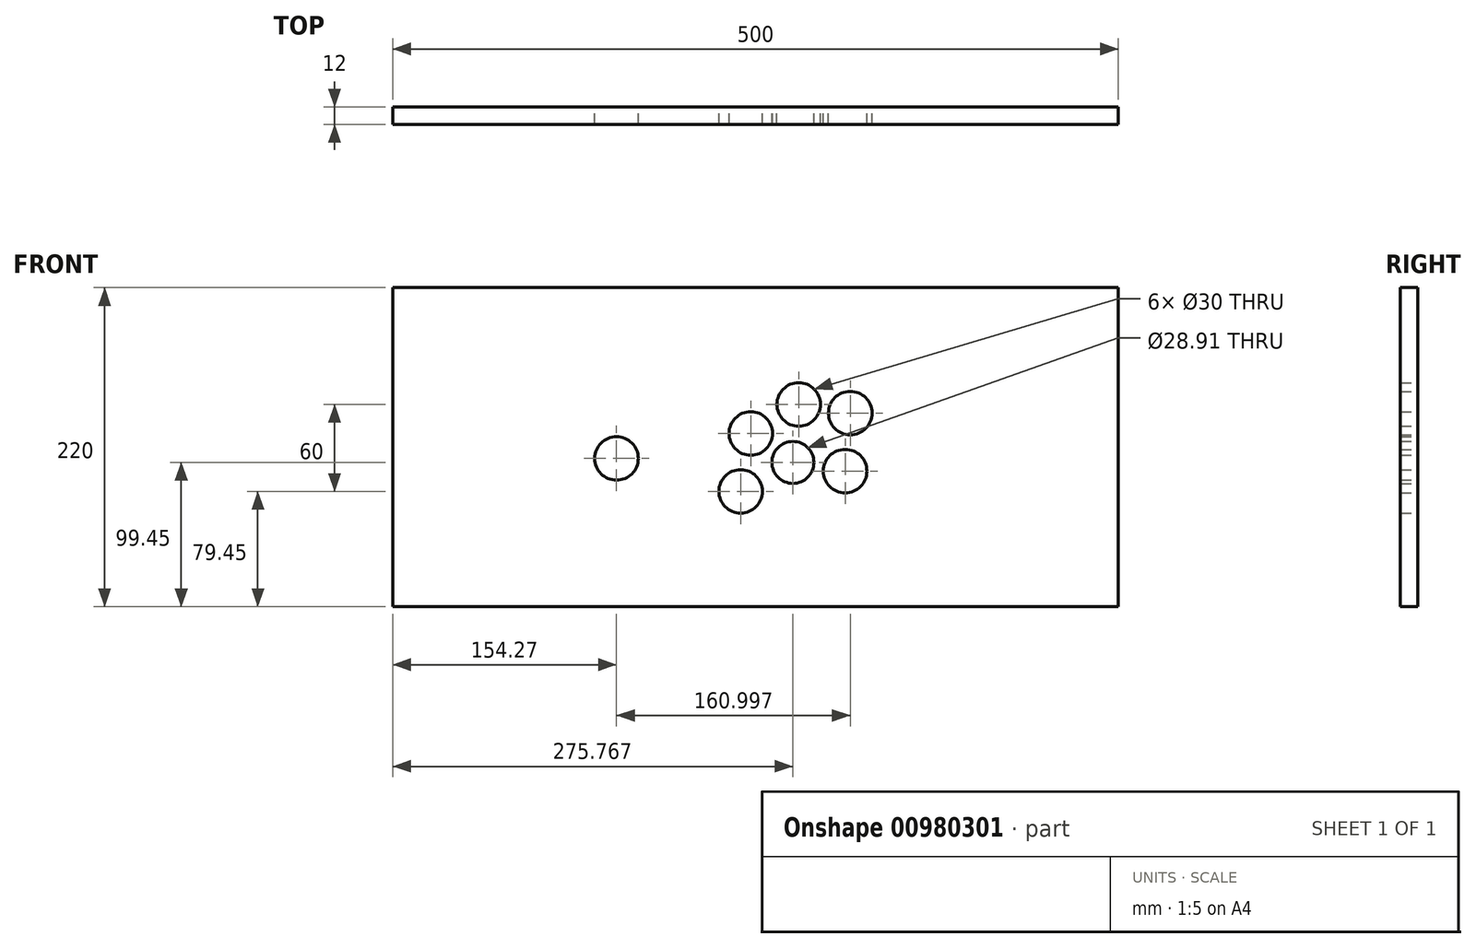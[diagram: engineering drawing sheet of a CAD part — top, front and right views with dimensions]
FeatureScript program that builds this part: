
annotation { "Feature Type Name" : "Feature", "Feature Type Description" : "" }
export const myFeature = defineFeature(function(context is Context, id is Id, definition is map)
    precondition{}
    {
        {
            var Q0;
            Q0=qCreatedBy(makeId("Front.planeOp"),FACE);
            var sketch = newSketch(context, id + "F0", { "sketchPlane" : qUnion([Q0])});
            skLineSegment(sketch, "E0.bottom", {"start": v(-244.54, 100.55) * mm, "end": v(255.46, 100.55) * mm});
            skLineSegment(sketch, "E0.top", {"start": v(-244.54, -119.45) * mm, "end": v(255.46, -119.45) * mm});
            skLineSegment(sketch, "E0.left", {"start": v(-244.54, 100.55) * mm, "end": v(-244.54, -119.45) * mm});
            skLineSegment(sketch, "E0.right", {"start": v(255.46, 100.55) * mm, "end": v(255.46, -119.45) * mm});
            skCircle(sketch, "E1", {"center": v(-90.27, -17.2) * mm, "radius": 15 * mm});
            skCircle(sketch, "E2", {"center": v(2.23, 0) * mm, "radius": 15 * mm});
            skCircle(sketch, "E3", {"center": v(35.23, 20) * mm, "radius": 15 * mm});
            skCircle(sketch, "E4", {"center": v(70.73, 14) * mm, "radius": 15 * mm});
            skCircle(sketch, "E5", {"center": v(-4.77, -40) * mm, "radius": 15 * mm});
            skCircle(sketch, "E6", {"center": v(31.23, -20) * mm, "radius": 14.46 * mm});
            skCircle(sketch, "E7", {"center": v(67.23, -26) * mm, "radius": 15 * mm});
            skSolve(sketch);
        }
        {
            var Q0;
            Q0 = qSketchRegion(id + "F0", true);
            extrude(context, id + "F1", {"entities" : qUnion([Q0]), "depth" : 12 * mm, "offsetDistance" : 25.4 * mm});
        }
    });
